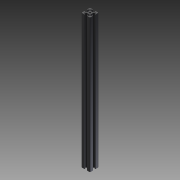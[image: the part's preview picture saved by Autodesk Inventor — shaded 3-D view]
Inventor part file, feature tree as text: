
AUTODESK INVENTOR PART (.ipt)
format: ipt  version: 2014 SP1 (Build 180222100, 222)  size: 171,520 bytes
history: native  units: mm
features: other x7, sketch x2, extrude x1, revolve x1
ambient origin geometry x8: Origin, YZ Plane, XZ Plane, XY Plane, X Axis, Y Axis, Z Axis, Center Point
bodies: Solid1 (feature_tree)
feature tree (11):
  extrude  "Extrusion1"  TaperAngle=360.0deg  [1 undecoded]
  revolve  "Revolution1"  [1 undecoded]
  other  "C1_XY"
  other  "C1_YZ"
  other  "C1_ZX"
  other  "C1_X"
  other  "C1_Y"
  other  "C1_Z"
  other  "C1_Center"
  sketch  "Sketch_1"  dims[d0=315.0mm d1=0.0mm d2=360.0deg]
  sketch  "Sketch_2"
note: 2 required parameter values undecoded (feature->parameter linkage not recoverable at this tier; creation-order binding heuristic only, values carry confidence <= 0.55)
